# Revit family: НЕВАТОМ_Решетка защитная ВР D, Версия 1
name_source: partatom
category: Арматура воздуховодов
revit_build: Autodesk Revit 2017 (Build: 20170118_1100(x64)
units: mm (PartAtom-declared; Revit-internal decimal feet)

## family parameters
Всегда вертикально = Нет
На основе рабочей плоскости = Нет
Общий = Нет
При загрузке вырезать с полостями = Нет
Размер круглого соединителя = Использовать диаметр
Тип детали = Вставляется

## types (9) — shared parameters
ADSK_Единица измерения = шт.
ADSK_Завод-изготовитель = НЕВАТОМ
ADSK_Количество = 1
ADSK_Наименование = Решетка защитная
материал = Сталь оцинкованная
ширина ободка = 5 мм
ширина решетки = 5 мм

## per-type parameters (varying)
| type | ADSK_Марка | D | D1 | Nevatom_URL | d | длина | ширина |
| Решетка защитная ВР круглая D260(2,0) | ВР-260 | 260 мм | 230 мм |  | 200 мм | 2000 мм | 2000 мм |
| Решетка защитная ВР круглая D1330(12,5) | ВР-1330 | 1330 мм | 1280 мм | https://t.me | 1230 мм | 1930 мм | 1930 мм |
| Решетка защитная ВР круглая D1080(10) | ВР-1080 | 1080 мм | 1032 мм | https://t.me | 984 мм | 1784 мм | 1784 мм |
| Решетка защитная ВР круглая D864(8) | ВР-864 | 864 мм | 832 мм | https://t.me | 800 мм | 1784 мм | 1784 мм |
| Решетка защитная ВР круглая D680(6,3) | ВР-680 | 680 мм | 655 мм | https://t.me | 630 мм | 1784 мм | 1784 мм |
| Решетка защитная ВР круглая D550(5) | ВР-550 | 550 мм | 525 мм | https://t.me | 500 мм | 1784 мм | 1784 мм |
| Решетка защитная ВР круглая D450(4) | ВР-450 | 450 мм | 425 мм | https://t.me | 400 мм | 1784 мм | 1784 мм |
| Решетка защитная ВР круглая D375(3,15) | ВР-375 | 375 мм | 345 мм | https://t.me | 315 мм | 1784 мм | 1784 мм |
| Решетка защитная ВР круглая D310(2,5) | ВР-310 | 310 мм | 280 мм | https://t.me | 250 мм | 1784 мм | 1784 мм |
